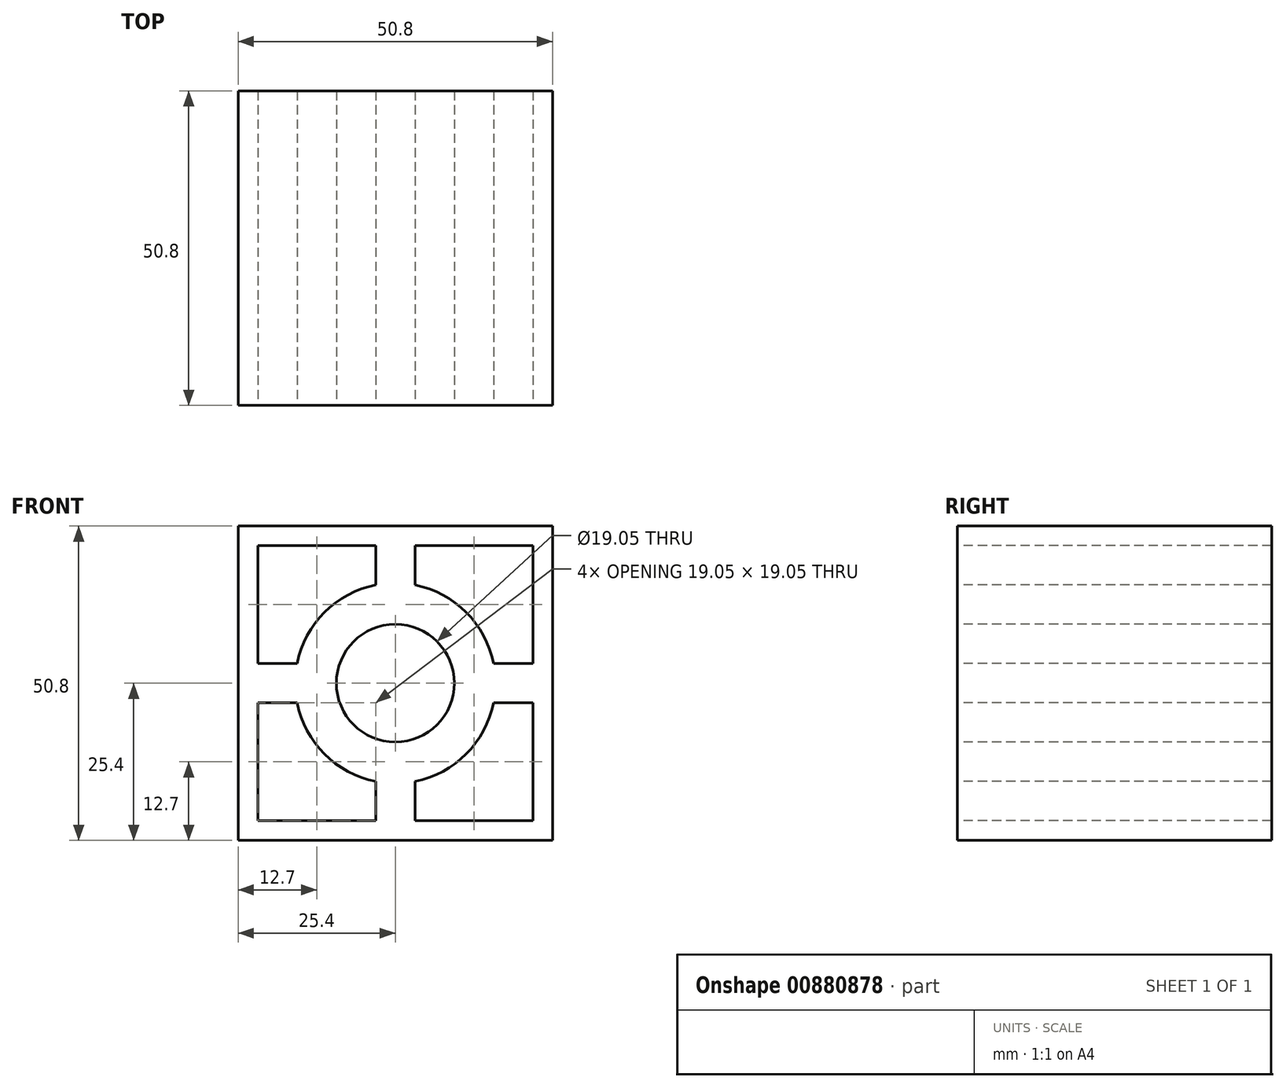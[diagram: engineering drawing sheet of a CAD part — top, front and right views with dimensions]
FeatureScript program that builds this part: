
annotation { "Feature Type Name" : "Feature", "Feature Type Description" : "" }
export const myFeature = defineFeature(function(context is Context, id is Id, definition is map)
    precondition{}
    {
        {
            var Q0;
            Q0=qCreatedBy(makeId("Front.planeOp"),FACE);
            var sketch = newSketch(context, id + "F0", { "sketchPlane" : qUnion([Q0])});
            skLineSegment(sketch, "E0", {"start": v(0, 0) * mm, "end": v(0, 50.8) * mm});
            skLineSegment(sketch, "E1", {"start": v(50.8, 50.8) * mm, "end": v(50.8, 0) * mm});
            skLineSegment(sketch, "E2", {"start": v(50.8, 0) * mm, "end": v(0, 0) * mm});
            skLineSegment(sketch, "E3", {"start": v(50.8, 50.8) * mm, "end": v(0, 50.8) * mm});
            skSolve(sketch);
        }
        {
            var Q0;
            Q0 = qSketchRegion(id + "F0", true);
            extrude(context, id + "F1", {"entities" : qUnion([Q0]), "depth" : 50.8 * mm, "offsetDistance" : 25.4 * mm});
        }
        {
            var Q0;
            Q0=makeQuery(id+"F1.opExtrude","CAP_FACE",FACE,{"disambiguationData":[OSD([sQuery(id+"F0.wireOp",EDGE,"E0"),sQuery(id+"F0.wireOp",EDGE,"E1"),sQuery(id+"F0.wireOp",EDGE,"E2"),sQuery(id+"F0.wireOp",EDGE,"E3")])],"isStart":false});
            var sketch = newSketch(context, id + "F2", { "sketchPlane" : qUnion([Q0])});
            skLineSegment(sketch, "E4", {"start": v(3.17, 47.62) * mm, "end": v(3.18, 28.57) * mm});
            skLineSegment(sketch, "E5", {"start": v(3.18, 28.57) * mm, "end": v(9.53, 28.57) * mm});
            skLineSegment(sketch, "E6", {"start": v(3.17, 47.62) * mm, "end": v(22.23, 47.62) * mm});
            skLineSegment(sketch, "E7", {"start": v(22.22, 47.62) * mm, "end": v(22.22, 41.27) * mm});
            skLineSegment(sketch, "E8", {"start": v(28.57, 47.62) * mm, "end": v(47.62, 47.62) * mm});
            skLineSegment(sketch, "E9", {"start": v(47.62, 47.62) * mm, "end": v(47.62, 28.58) * mm});
            skLineSegment(sketch, "E10", {"start": v(47.62, 28.58) * mm, "end": v(41.28, 28.58) * mm});
            skLineSegment(sketch, "E11", {"start": v(28.58, 47.62) * mm, "end": v(28.58, 41.27) * mm});
            skLineSegment(sketch, "E12", {"start": v(22.22, 9.52) * mm, "end": v(22.22, 3.17) * mm});
            skLineSegment(sketch, "E13", {"start": v(22.23, 3.17) * mm, "end": v(3.18, 3.17) * mm});
            skLineSegment(sketch, "E14", {"start": v(3.18, 3.17) * mm, "end": v(3.18, 22.22) * mm});
            skLineSegment(sketch, "E15", {"start": v(3.18, 22.22) * mm, "end": v(9.53, 22.22) * mm});
            skLineSegment(sketch, "E16", {"start": v(41.28, 22.22) * mm, "end": v(47.63, 22.22) * mm});
            skLineSegment(sketch, "E17", {"start": v(47.63, 22.22) * mm, "end": v(47.63, 3.17) * mm});
            skLineSegment(sketch, "E18", {"start": v(47.63, 3.17) * mm, "end": v(28.58, 3.17) * mm});
            skLineSegment(sketch, "E19", {"start": v(28.58, 3.17) * mm, "end": v(28.58, 9.52) * mm});
            skArc(sketch, "E20", {"start": v(22.23, 41.27) * mm, "mid": v(13.95, 36.85) * mm, "end": v(9.53, 28.58) * mm});
            skArc(sketch, "E21", {"start": v(41.28, 28.58) * mm, "mid": v(36.85, 36.85) * mm, "end": v(28.58, 41.27) * mm});
            skArc(sketch, "E22", {"start": v(28.58, 9.52) * mm, "mid": v(36.85, 13.95) * mm, "end": v(41.28, 22.22) * mm});
            skArc(sketch, "E23", {"start": v(9.52, 22.22) * mm, "mid": v(13.95, 13.95) * mm, "end": v(22.23, 9.52) * mm});
            skCircle(sketch, "E24", {"center": v(25.4, 25.4) * mm, "radius": 9.53 * mm});
            skSolve(sketch);
        }
        {
            var Q0;
            Q0 = qSketchRegion(id + "F2", true);
            extrude(context, id + "F3", {"entities" : qUnion([Q0]), "operationType" : NewBodyOperationType.REMOVE, "endBound" : BoundingType.THROUGH_ALL, "oppositeDirection" : true, "depth" : 25.4 * mm, "offsetDistance" : 25.4 * mm});
        }
    });
